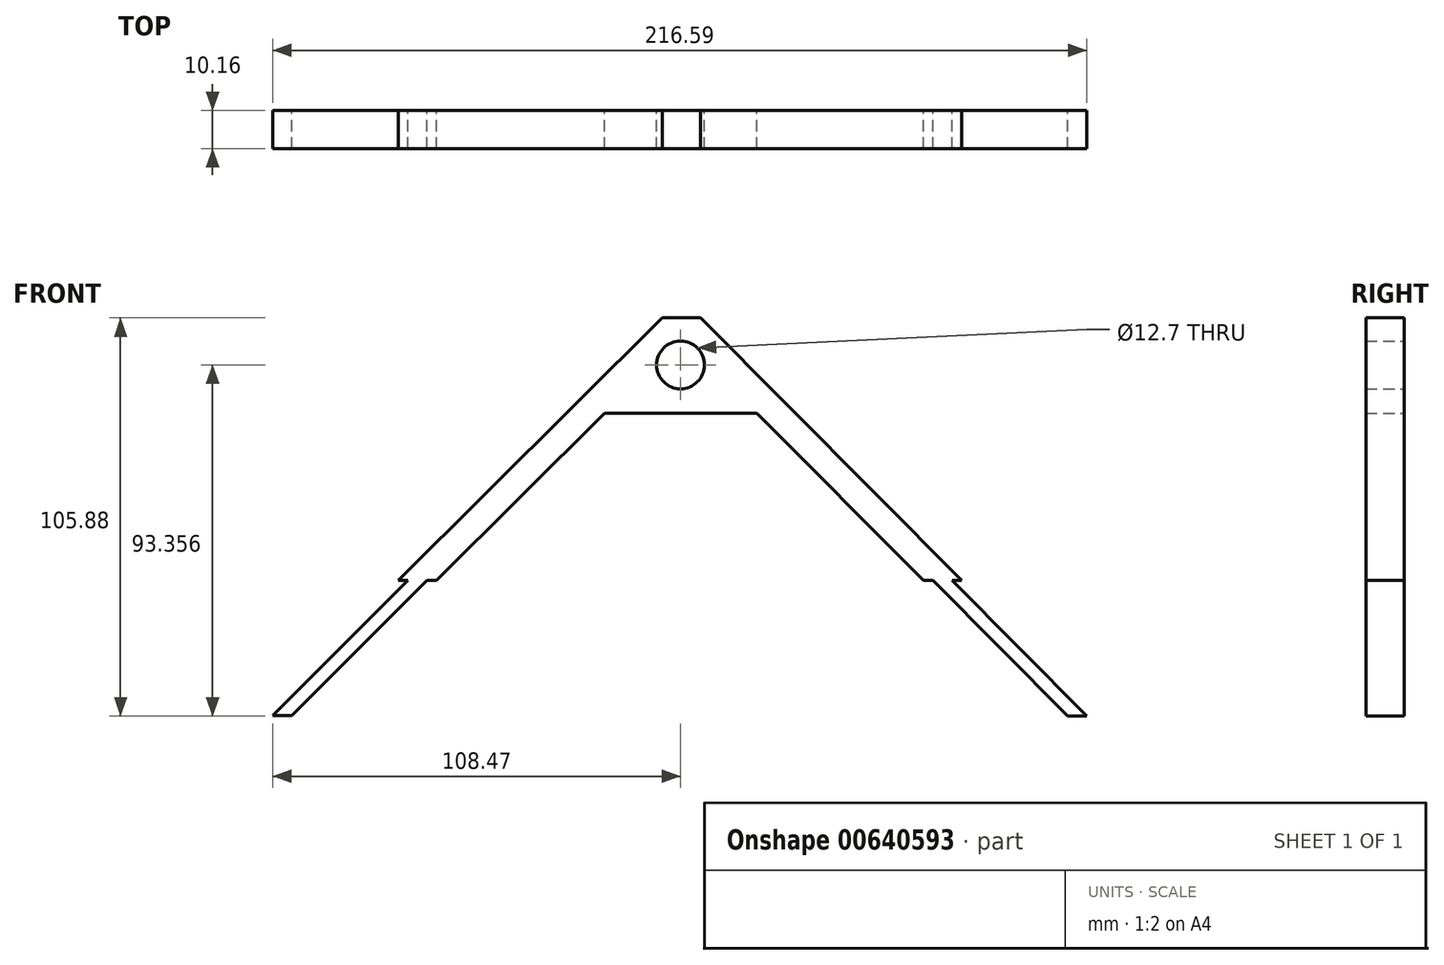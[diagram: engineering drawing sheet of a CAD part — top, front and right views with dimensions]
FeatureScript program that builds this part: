
annotation { "Feature Type Name" : "Feature", "Feature Type Description" : "" }
export const myFeature = defineFeature(function(context is Context, id is Id, definition is map)
    precondition{}
    {
        {
            var Q0;
            Q0=qCreatedBy(makeId("Front.planeOp"),FACE);
            var sketch = newSketch(context, id + "F0", { "sketchPlane" : qUnion([Q0])});
            skPoint(sketch, "E0", {"position": v(-75.1, 1.33) * mm});
            skLineSegment(sketch, "E1", {"start": v(-75.1, 1.33) * mm, "end": v(-4.87, 71.2) * mm});
            skLineSegment(sketch, "E2", {"start": v(-4.87, 71.2) * mm, "end": v(5.29, 71.2) * mm});
            skLineSegment(sketch, "E3", {"start": v(5.29, 71.2) * mm, "end": v(74.82, 1.33) * mm});
            skCircle(sketch, "E4", {"center": v(0, 58.68) * mm, "radius": 6.35 * mm});
            skLineSegment(sketch, "E5", {"start": v(-4.94, 45.87) * mm, "end": v(5.29, 45.87) * mm});
            skLineSegment(sketch, "E6", {"start": v(-64.93, 1.33) * mm, "end": v(-20.18, 45.87) * mm});
            skLineSegment(sketch, "E7", {"start": v(-20.18, 45.87) * mm, "end": v(-4.94, 45.87) * mm});
            skLineSegment(sketch, "E8", {"start": v(64.66, 1.33) * mm, "end": v(20.34, 45.87) * mm});
            skLineSegment(sketch, "E9", {"start": v(20.34, 45.87) * mm, "end": v(5.29, 45.87) * mm});
            skLineSegment(sketch, "E10", {"start": v(64.66, 1.33) * mm, "end": v(67.2, 1.33) * mm});
            skLineSegment(sketch, "E11", {"start": v(74.82, 1.33) * mm, "end": v(72.27, 1.32) * mm});
            skLineSegment(sketch, "E12", {"start": v(103.04, -34.68) * mm, "end": v(67.2, 1.33) * mm});
            skLineSegment(sketch, "E13", {"start": v(72.27, 1.32) * mm, "end": v(108.12, -34.68) * mm});
            skLineSegment(sketch, "E14", {"start": v(103.04, -34.68) * mm, "end": v(108.12, -34.68) * mm});
            skLineSegment(sketch, "E15", {"start": v(-67.47, 1.33) * mm, "end": v(-64.93, 1.33) * mm});
            skLineSegment(sketch, "E16", {"start": v(-72.55, 1.33) * mm, "end": v(-75.1, 1.33) * mm});
            skLineSegment(sketch, "E17", {"start": v(-72.55, 1.33) * mm, "end": v(-108.47, -34.6) * mm});
            skLineSegment(sketch, "E18", {"start": v(-67.47, 1.33) * mm, "end": v(-103.4, -34.6) * mm});
            skLineSegment(sketch, "E19", {"start": v(-108.47, -34.6) * mm, "end": v(-103.4, -34.6) * mm});
            skSolve(sketch);
        }
        {
            var Q0;
            {var subQ2=sQuery(id+"F0.wireOp",EDGE,"E1");Q0=makeQuery(id+"F0.imprint","IMPRINT",FACE,{"disambiguationData":[TD([[makeQuery(id+"F0.imprint","IMPRINT",EDGE,{"derivedFrom":subQ2}),-1.0]])]});}
            var Q1;
            Q1=makeQuery(id+"F0.imprint","IMPRINT",FACE,{"disambiguationData":[TD([[makeQuery(id+"F0.imprint","IMPRINT",EDGE,{"derivedFrom":sQuery(id+"F0.wireOp",EDGE,"wpYTy7sd-HpSi-w1Er-A0oa-9MDZLQ8jqnZ0")}),1.0]])]});
            var Q2;
            Q2=makeQuery(id+"F0.imprint","IMPRINT",FACE,{"disambiguationData":[TD([[makeQuery(id+"F0.imprint","IMPRINT",EDGE,{"derivedFrom":sQuery(id+"F0.wireOp",EDGE,"U3wxSxf6-Yrtl-wJfo-I3fQ-b3RtTAKliQwI")}),1.0]])]});
            extrude(context, id + "F1", {"entities" : qUnion([Q0, Q1, Q2]), "depth" : 10.16 * mm, "offsetDistance" : 25.4 * mm});
        }
    });
